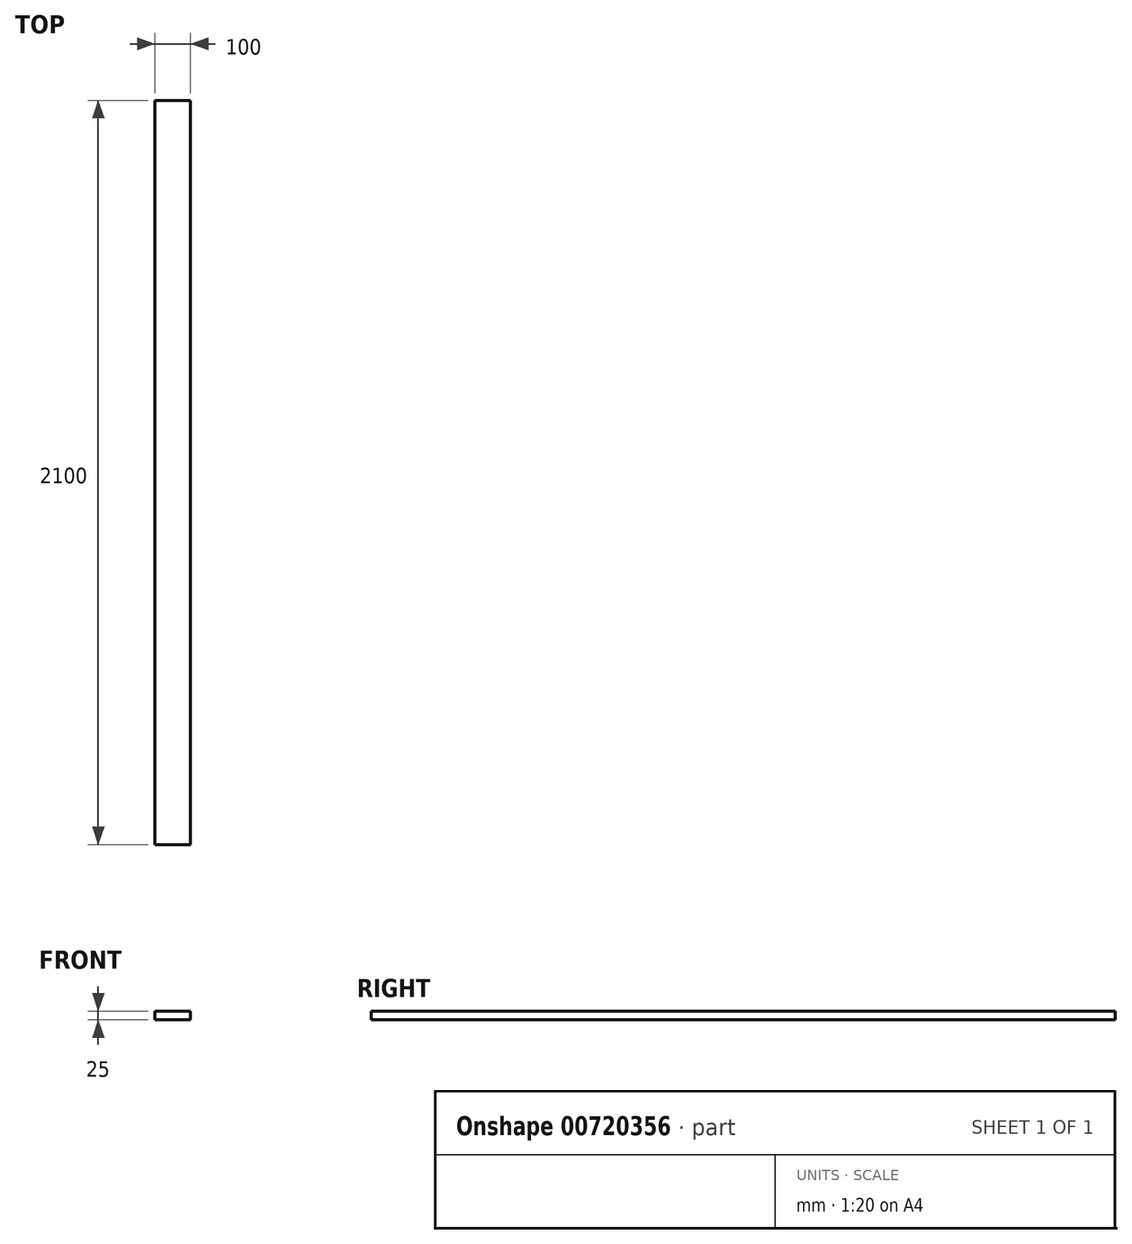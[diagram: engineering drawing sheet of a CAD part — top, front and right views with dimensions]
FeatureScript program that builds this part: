
annotation { "Feature Type Name" : "Feature", "Feature Type Description" : "" }
export const myFeature = defineFeature(function(context is Context, id is Id, definition is map)
    precondition{}
    {
        {
            var Q0;
            Q0=qCreatedBy(makeId("Top.planeOp"),FACE);
            var sketch = newSketch(context, id + "F0", { "sketchPlane" : qUnion([Q0])});
            skLineSegment(sketch, "E0.bottom", {"start": v(-50, 1000) * mm, "end": v(50, 1000) * mm});
            skLineSegment(sketch, "E0.top", {"start": v(-50, -1000) * mm, "end": v(50, -1000) * mm});
            skLineSegment(sketch, "E0.left", {"start": v(-50, 1000) * mm, "end": v(-50, -1000) * mm});
            skLineSegment(sketch, "E0.right", {"start": v(50, 1000) * mm, "end": v(50, -1000) * mm});
            skPoint(sketch, "E0.middle", {"position": v(0, 0) * mm});
            skSolve(sketch);
        }
        {
            var Q0;
            Q0 = qSketchRegion(id + "F0", true);
            extrude(context, id + "F1", {"entities" : qUnion([Q0]), "depth" : 50 * mm, "offsetDistance" : 25 * mm});
        }
        {
            var Q0;
            Q0=makeQuery(id+"F1.opExtrude","SWEPT_FACE",FACE,{"disambiguationData":[OSD([sQuery(id+"F0.wireOp",EDGE,"E0.top")])]});
            extrude(context, id + "F2", {"entities" : qUnion([Q0]), "operationType" : NewBodyOperationType.ADD, "depth" : 100 * mm, "offsetDistance" : 25 * mm});
        }
        {
            var Q0;
            {var subQ0=sQuery(id+"F0.wireOp",EDGE,"E0.top");Q0=makeQuery(id+"F2.boolean.opBoolean","MERGE",FACE,{"derivedFrom":[makeQuery(id+"F1.opExtrude","CAP_FACE",FACE,{"disambiguationData":[OSD([sQuery(id+"F0.wireOp",EDGE,"E0.bottom"),subQ0,sQuery(id+"F0.wireOp",EDGE,"E0.left"),sQuery(id+"F0.wireOp",EDGE,"E0.right")])],"isStart":false}),makeQuery(id+"F2.opExtrude","SWEPT_FACE",FACE,{"disambiguationData":[OSD([subQ0]),TDD([makeQuery(id+"F1.opExtrude","CAP_EDGE",EDGE,{"disambiguationData":[OSD([subQ0])],"isStart":false})])]})]});}
            extrude(context, id + "F3", {"entities" : qUnion([Q0]), "operationType" : NewBodyOperationType.REMOVE, "oppositeDirection" : true, "depth" : 25 * mm, "offsetDistance" : 25 * mm});
        }
    });
